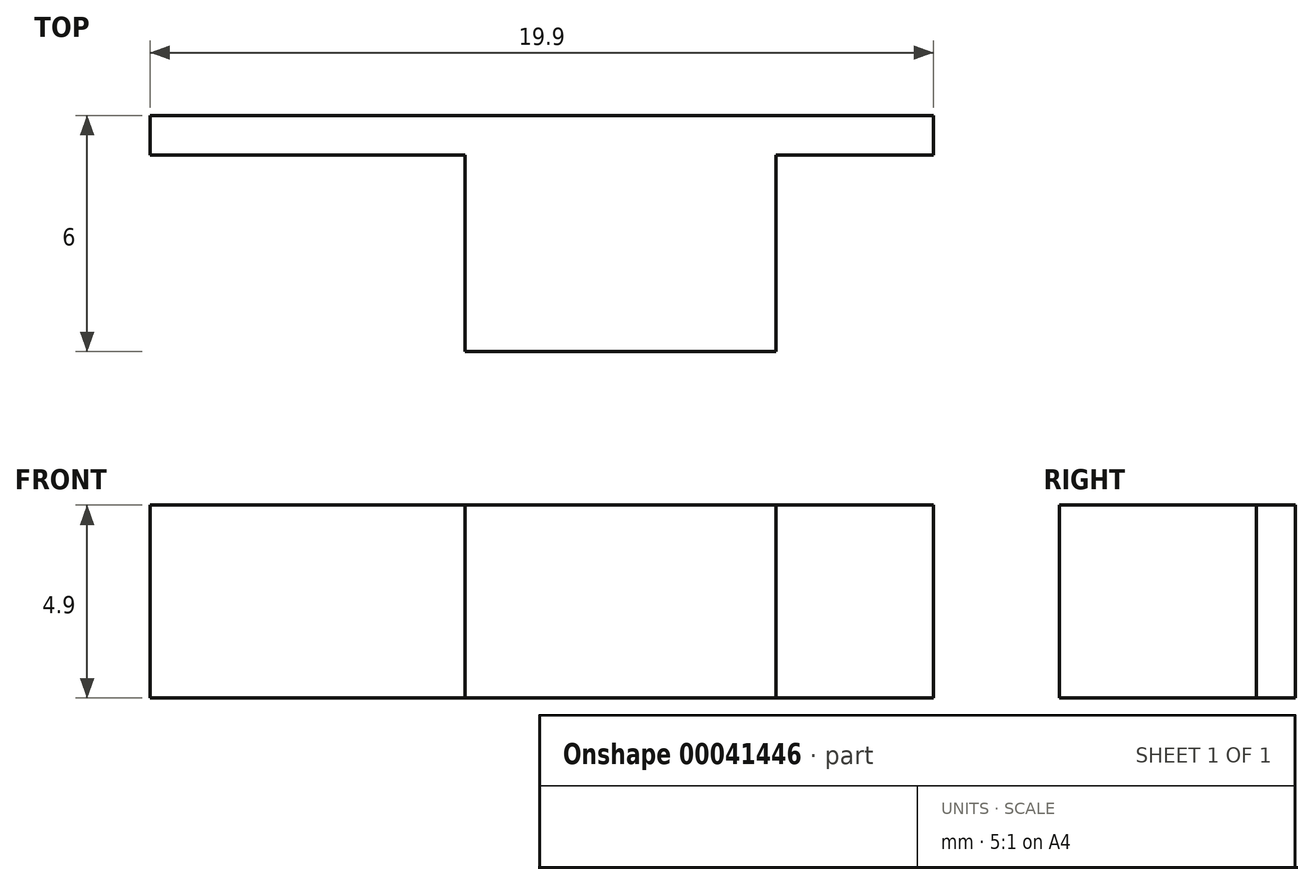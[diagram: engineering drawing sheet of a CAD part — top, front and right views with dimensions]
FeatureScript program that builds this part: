
annotation { "Feature Type Name" : "Feature", "Feature Type Description" : "" }
export const myFeature = defineFeature(function(context is Context, id is Id, definition is map)
    precondition{}
    {
        {
            var Q0;
            Q0=qCreatedBy(makeId("Top.planeOp"),FACE);
            var sketch = newSketch(context, id + "F0", { "sketchPlane" : qUnion([Q0])});
            skLineSegment(sketch, "E0.rect.bottom", {"start": v(3.95, 2.5) * mm, "end": v(-3.95, 2.5) * mm});
            skLineSegment(sketch, "E0.rect.top", {"start": v(3.95, -2.5) * mm, "end": v(-3.95, -2.5) * mm});
            skLineSegment(sketch, "E0.rect.left", {"start": v(3.95, 2.5) * mm, "end": v(3.95, -2.5) * mm});
            skLineSegment(sketch, "E0.rect.right", {"start": v(-3.95, 2.5) * mm, "end": v(-3.95, -2.5) * mm});
            skPoint(sketch, "E0.rect.middle", {"position": v(0, 0) * mm});
            skLineSegment(sketch, "E1.bottom", {"start": v(-11.95, 2.5) * mm, "end": v(7.95, 2.5) * mm});
            skLineSegment(sketch, "E1.top", {"start": v(-11.95, 3.5) * mm, "end": v(7.95, 3.5) * mm});
            skLineSegment(sketch, "E1.left", {"start": v(-11.95, 2.5) * mm, "end": v(-11.95, 3.5) * mm});
            skLineSegment(sketch, "E1.right", {"start": v(7.95, 2.5) * mm, "end": v(7.95, 3.5) * mm});
            skLineSegment(sketch, "E2.bottom", {"start": v(3.95, 3.5) * mm, "end": v(-4.05, 3.5) * mm});
            skLineSegment(sketch, "E2.left", {"start": v(3.95, 3.5) * mm, "end": v(3.95, 11.5) * mm});
            skLineSegment(sketch, "E3", {"start": v(3.95, 11.5) * mm, "end": v(-3.45, 11.5) * mm});
            skLineSegment(sketch, "E4", {"start": v(-3.45, 11.5) * mm, "end": v(-4.05, 3.5) * mm});
            skSolve(sketch);
        }
        {
            var Q0;
            Q0=makeQuery(id+"F0.imprint","IMPRINT",FACE,{"disambiguationData":[TD([[makeQuery(id+"F0.imprint","IMPRINT",EDGE,{"derivedFrom":sQuery(id+"F0.wireOp",EDGE,"E0.rect.top")}),-1.0]])]});
            var Q1;
            {var subQ1=sQuery(id+"F0.wireOp",EDGE,"E1.left");Q1=makeQuery(id+"F0.imprint","IMPRINT",FACE,{"disambiguationData":[TD([[makeQuery(id+"F0.imprint","IMPRINT",EDGE,{"derivedFrom":subQ1}),-1.0]])]});}
            var Q2;
            Q2=makeQuery(id+"F0.imprint","IMPRINT",FACE,{"disambiguationData":[TD([[makeQuery(id+"F0.imprint","IMPRINT",EDGE,{"derivedFrom":sQuery(id+"F0.wireOp",EDGE,"E2.bottom")}),-1.0]])]});
            extrude(context, id + "F1", {"entities" : qUnion([Q0, Q1, Q2]), "depth" : 4.9 * mm});
        }
    });
